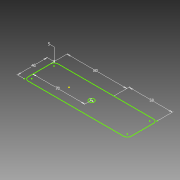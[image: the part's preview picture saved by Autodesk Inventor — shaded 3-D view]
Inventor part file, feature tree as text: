
AUTODESK INVENTOR PART (.ipt)
format: ipt  version: 2012 (Build 160160000, 160)  size: 67,072 bytes
history: native  units: mm
features: sketch x1
ambient origin geometry x8: Origin, YZ Plane, XZ Plane, XY Plane, X Axis, Y Axis, Z Axis, Center Point
feature tree (1):
  sketch  "Sketch1"  dims[d1=7.0mm d36=40.0mm d38=58.0mm d47=80.0mm d49=5.0mm d52=70.0mm]
